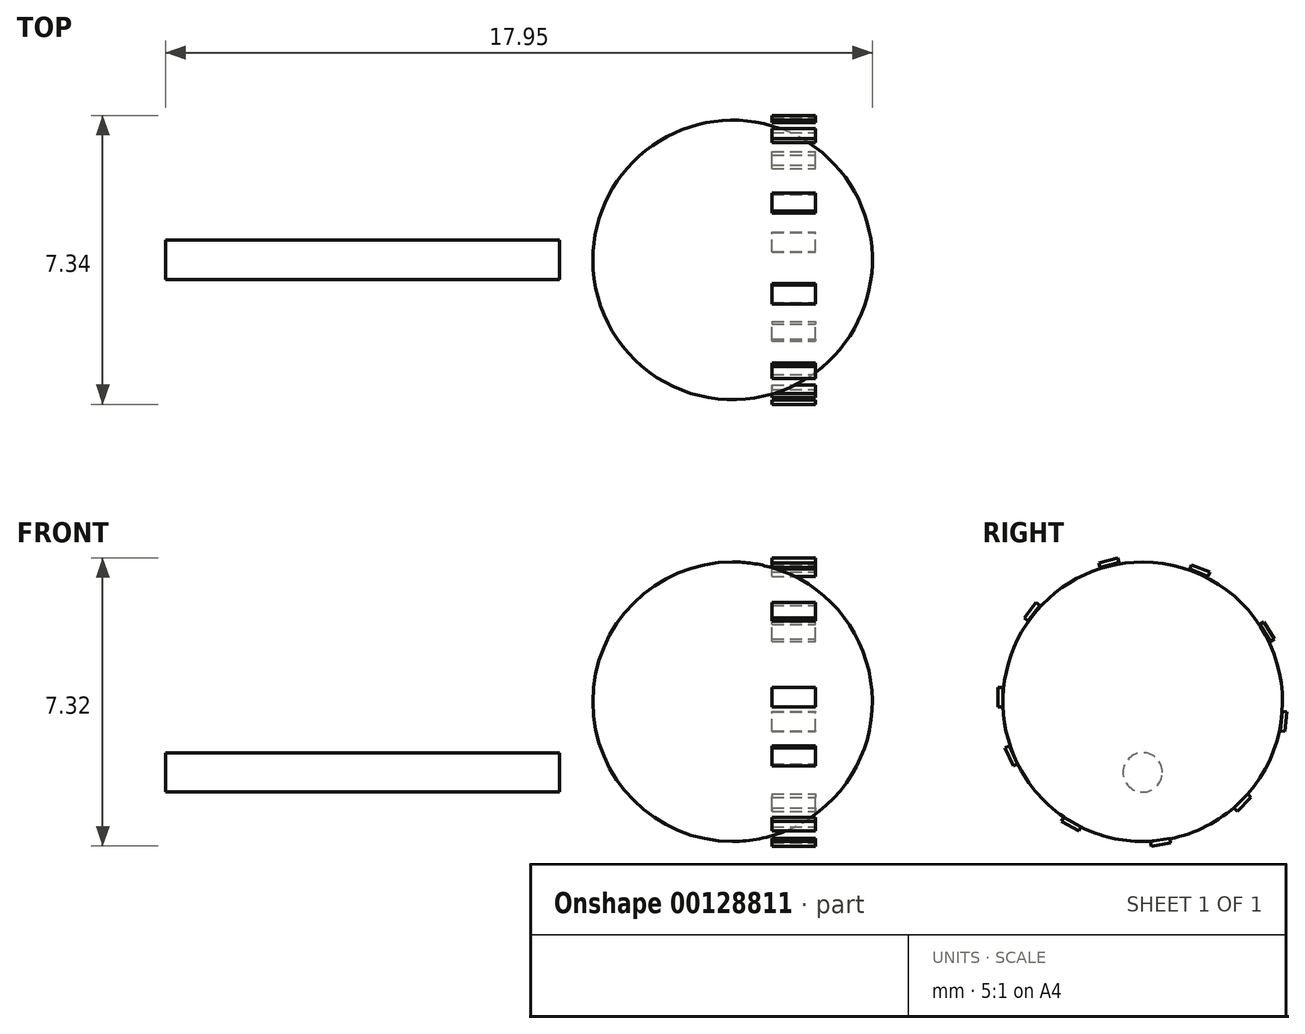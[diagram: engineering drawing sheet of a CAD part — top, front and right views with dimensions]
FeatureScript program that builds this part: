
annotation { "Feature Type Name" : "Feature", "Feature Type Description" : "" }
export const myFeature = defineFeature(function(context is Context, id is Id, definition is map)
    precondition{}
    {
        {
            var Q0;
            Q0=qCreatedBy(makeId("Front.planeOp"),FACE);
            var sketch = newSketch(context, id + "F0", { "sketchPlane" : qUnion([Q0])});
            skLineSegment(sketch, "E0", {"start": v(0, 35.6) * mm, "end": v(0, 28.5) * mm});
            skArc(sketch, "E1", {"start": v(0, 35.6) * mm, "mid": v(3.55, 32.06) * mm, "end": v(0, 28.5) * mm});
            skSolve(sketch);
        }
        {
            var Q0;
            Q0 = qSketchRegion(id + "F0", true);
            var Q1;
            Q1=sQuery(id+"F0.wireOp",EDGE,"E0");
            revolve(context, id + "F1", {"entities" : qUnion([Q0]), "axis" : qUnion([Q1]), "revolveType" : RevolveType.FULL});
        }
        {
            var Q0;
            Q0=qCreatedBy(makeId("Right.planeOp"),FACE);
            cPlane(context, id + "F2", {"entities" : qUnion([Q0]), "cplaneType" : CPlaneType.OFFSET, "offset" : 4.4 * mm, "oppositeDirection" : true, "width" : 150 * mm, "height" : 150 * mm});
        }
        {
            var Q0;
            Q0=qCreatedBy(id+"F2.planeOp",FACE);
            var sketch = newSketch(context, id + "F3", { "sketchPlane" : qUnion([Q0])});
            skCircle(sketch, "E2", {"center": v(0, 30.26) * mm, "radius": 0.5 * mm});
            skSolve(sketch);
        }
        {
            var Q0;
            Q0 = qSketchRegion(id + "F3", true);
            extrude(context, id + "F4", {"entities" : qUnion([Q0]), "oppositeDirection" : true, "depth" : 10 * mm});
        }
        {
            var Q0;
            Q0=qCreatedBy(makeId("Top.planeOp"),FACE);
            cPlane(context, id + "F5", {"entities" : qUnion([Q0]), "cplaneType" : CPlaneType.OFFSET, "offset" : 35.7 * mm, "width" : 150 * mm, "height" : 150 * mm});
        }
        {
            var Q0;
            Q0=qCreatedBy(id+"F2.planeOp",FACE);
            cPlane(context, id + "F6", {"entities" : qUnion([Q0]), "cplaneType" : CPlaneType.OFFSET, "offset" : 2.5 * mm, "width" : 150 * mm, "height" : 150 * mm});
        }
        {
            var Q0;
            Q0=qCreatedBy(id+"F6.planeOp",FACE);
            cPlane(context, id + "F7", {"entities" : qUnion([Q0]), "cplaneType" : CPlaneType.OFFSET, "offset" : 4 * mm, "width" : 150 * mm, "height" : 150 * mm});
        }
        {
            var Q0;
            Q0=qCreatedBy(id+"F7.planeOp",FACE);
            var sketch = newSketch(context, id + "F8", { "sketchPlane" : qUnion([Q0])});
            skPoint(sketch, "E3.center", {"position": v(0, 31.75) * mm});
            skLineSegment(sketch, "E4.bottom", {"start": v(-3.56, 32.43) * mm, "end": v(-3.67, 32.43) * mm});
            skLineSegment(sketch, "E4.top", {"start": v(-3.56, 31.93) * mm, "end": v(-3.67, 31.93) * mm});
            skLineSegment(sketch, "E4.left", {"start": v(-3.56, 32.43) * mm, "end": v(-3.56, 31.93) * mm});
            skLineSegment(sketch, "E4.right", {"start": v(-3.67, 32.43) * mm, "end": v(-3.67, 31.93) * mm});
            skLineSegment(sketch, "E5.1.0", {"start": v(-2.7, 34.58) * mm, "end": v(-3.01, 34.18) * mm});
            skLineSegment(sketch, "E5.1.1", {"start": v(-2.92, 34.11) * mm, "end": v(-3.01, 34.18) * mm});
            skLineSegment(sketch, "E5.1.2", {"start": v(-2.61, 34.5) * mm, "end": v(-2.7, 34.58) * mm});
            skLineSegment(sketch, "E5.1.3", {"start": v(-2.61, 34.5) * mm, "end": v(-2.92, 34.11) * mm});
            skPoint(sketch, "E5.1.4", {"position": v(-0.2, 31.82) * mm});
            skLineSegment(sketch, "E5.2.0", {"start": v(-0.63, 35.7) * mm, "end": v(-1.12, 35.58) * mm});
            skLineSegment(sketch, "E5.2.1", {"start": v(-1.08, 35.46) * mm, "end": v(-1.12, 35.58) * mm});
            skLineSegment(sketch, "E5.2.2", {"start": v(-0.6, 35.6) * mm, "end": v(-0.63, 35.7) * mm});
            skLineSegment(sketch, "E5.2.3", {"start": v(-0.6, 35.6) * mm, "end": v(-1.08, 35.46) * mm});
            skPoint(sketch, "E5.2.4", {"position": v(-0.3, 31.99) * mm});
            skLineSegment(sketch, "E5.3.0", {"start": v(1.7, 35.35) * mm, "end": v(1.24, 35.53) * mm});
            skLineSegment(sketch, "E5.3.1", {"start": v(1.2, 35.42) * mm, "end": v(1.24, 35.53) * mm});
            skLineSegment(sketch, "E5.3.2", {"start": v(1.66, 35.24) * mm, "end": v(1.7, 35.35) * mm});
            skLineSegment(sketch, "E5.3.3", {"start": v(1.66, 35.24) * mm, "end": v(1.2, 35.42) * mm});
            skPoint(sketch, "E5.3.4", {"position": v(-0.3, 32.2) * mm});
            skLineSegment(sketch, "E5.4.0", {"start": v(3.34, 33.65) * mm, "end": v(3.08, 34.08) * mm});
            skLineSegment(sketch, "E5.4.1", {"start": v(2.98, 34.02) * mm, "end": v(3.08, 34.08) * mm});
            skLineSegment(sketch, "E5.4.2", {"start": v(3.24, 33.59) * mm, "end": v(3.34, 33.65) * mm});
            skLineSegment(sketch, "E5.4.3", {"start": v(3.24, 33.59) * mm, "end": v(2.98, 34.02) * mm});
            skPoint(sketch, "E5.4.4", {"position": v(-0.16, 32.35) * mm});
            skLineSegment(sketch, "E5.5.0", {"start": v(3.61, 31.3) * mm, "end": v(3.67, 31.8) * mm});
            skLineSegment(sketch, "E5.5.1", {"start": v(3.55, 31.81) * mm, "end": v(3.67, 31.8) * mm});
            skLineSegment(sketch, "E5.5.2", {"start": v(3.5, 31.32) * mm, "end": v(3.61, 31.3) * mm});
            skLineSegment(sketch, "E5.5.3", {"start": v(3.5, 31.32) * mm, "end": v(3.55, 31.81) * mm});
            skPoint(sketch, "E5.5.4", {"position": v(0.04, 32.4) * mm});
            skLineSegment(sketch, "E5.6.0", {"start": v(2.4, 29.27) * mm, "end": v(2.75, 29.63) * mm});
            skLineSegment(sketch, "E5.6.1", {"start": v(2.67, 29.71) * mm, "end": v(2.75, 29.63) * mm});
            skLineSegment(sketch, "E5.6.2", {"start": v(2.32, 29.35) * mm, "end": v(2.4, 29.27) * mm});
            skLineSegment(sketch, "E5.6.3", {"start": v(2.32, 29.35) * mm, "end": v(2.67, 29.71) * mm});
            skPoint(sketch, "E5.6.4", {"position": v(0.22, 32.3) * mm});
            skLineSegment(sketch, "E5.7.0", {"start": v(0.22, 28.39) * mm, "end": v(0.7, 28.46) * mm});
            skLineSegment(sketch, "E5.7.1", {"start": v(0.7, 28.58) * mm, "end": v(0.7, 28.46) * mm});
            skLineSegment(sketch, "E5.7.2", {"start": v(0.2, 28.5) * mm, "end": v(0.22, 28.39) * mm});
            skLineSegment(sketch, "E5.7.3", {"start": v(0.2, 28.5) * mm, "end": v(0.7, 28.58) * mm});
            skPoint(sketch, "E5.7.4", {"position": v(0.32, 32.12) * mm});
            skLineSegment(sketch, "E5.8.0", {"start": v(-2.06, 29) * mm, "end": v(-1.62, 28.77) * mm});
            skLineSegment(sketch, "E5.8.1", {"start": v(-1.57, 28.88) * mm, "end": v(-1.62, 28.77) * mm});
            skLineSegment(sketch, "E5.8.2", {"start": v(-2, 29.11) * mm, "end": v(-2.06, 29) * mm});
            skLineSegment(sketch, "E5.8.3", {"start": v(-2, 29.11) * mm, "end": v(-1.57, 28.88) * mm});
            skPoint(sketch, "E5.8.4", {"position": v(0.28, 31.92) * mm});
            skLineSegment(sketch, "E5.9.0", {"start": v(-3.5, 30.89) * mm, "end": v(-3.3, 30.43) * mm});
            skLineSegment(sketch, "E5.9.1", {"start": v(-3.18, 30.48) * mm, "end": v(-3.3, 30.43) * mm});
            skLineSegment(sketch, "E5.9.2", {"start": v(-3.39, 30.93) * mm, "end": v(-3.5, 30.89) * mm});
            skLineSegment(sketch, "E5.9.3", {"start": v(-3.39, 30.93) * mm, "end": v(-3.18, 30.48) * mm});
            skPoint(sketch, "E5.9.4", {"position": v(0.13, 31.78) * mm});
            skPoint(sketch, "E5.center", {"position": v(0, 32.07) * mm});
            skLineSegment(sketch, "E5.anchor1", {"start": v(0, 32.07) * mm, "end": v(-3.67, 31.93) * mm, "construction": true});
            skLineSegment(sketch, "E5.anchor2", {"start": v(0, 32.07) * mm, "end": v(-3.3, 30.43) * mm, "construction": true});
            skSolve(sketch);
        }
        {
            var Q0;
            Q0 = qSketchRegion(id + "F8", true);
            extrude(context, id + "F9", {"entities" : qUnion([Q0]), "oppositeDirection" : true, "depth" : 1.1 * mm});
        }
    });
